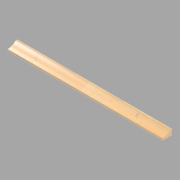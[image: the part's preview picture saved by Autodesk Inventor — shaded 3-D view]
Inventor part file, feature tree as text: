
AUTODESK INVENTOR PART (.ipt)
format: ipt  version: 2022.2 (Build 262287010, 287A)  size: 122,880 bytes
history: native  units: in
note: dims shown in document units (in); Inventor stores cm internally (conversion verified against a paired STEP export)
features: revolve x2, other x1, direct_edit x1
ambient origin geometry x8: Origin, YZ Plane, XZ Plane, XY Plane, X Axis, Y Axis, Z Axis, Center Point
bodies: Solid1 (feature_tree)
feature tree (4):
  other  "North (3)"
  direct_edit  "Direct Edit1"
  revolve  "Rotate1"  [1 undecoded]
  revolve  "Rotate2"  Angle=90.0deg
note: 1 required parameter value undecoded (feature->parameter linkage not recoverable at this tier; creation-order binding heuristic only, values carry confidence <= 0.55)
